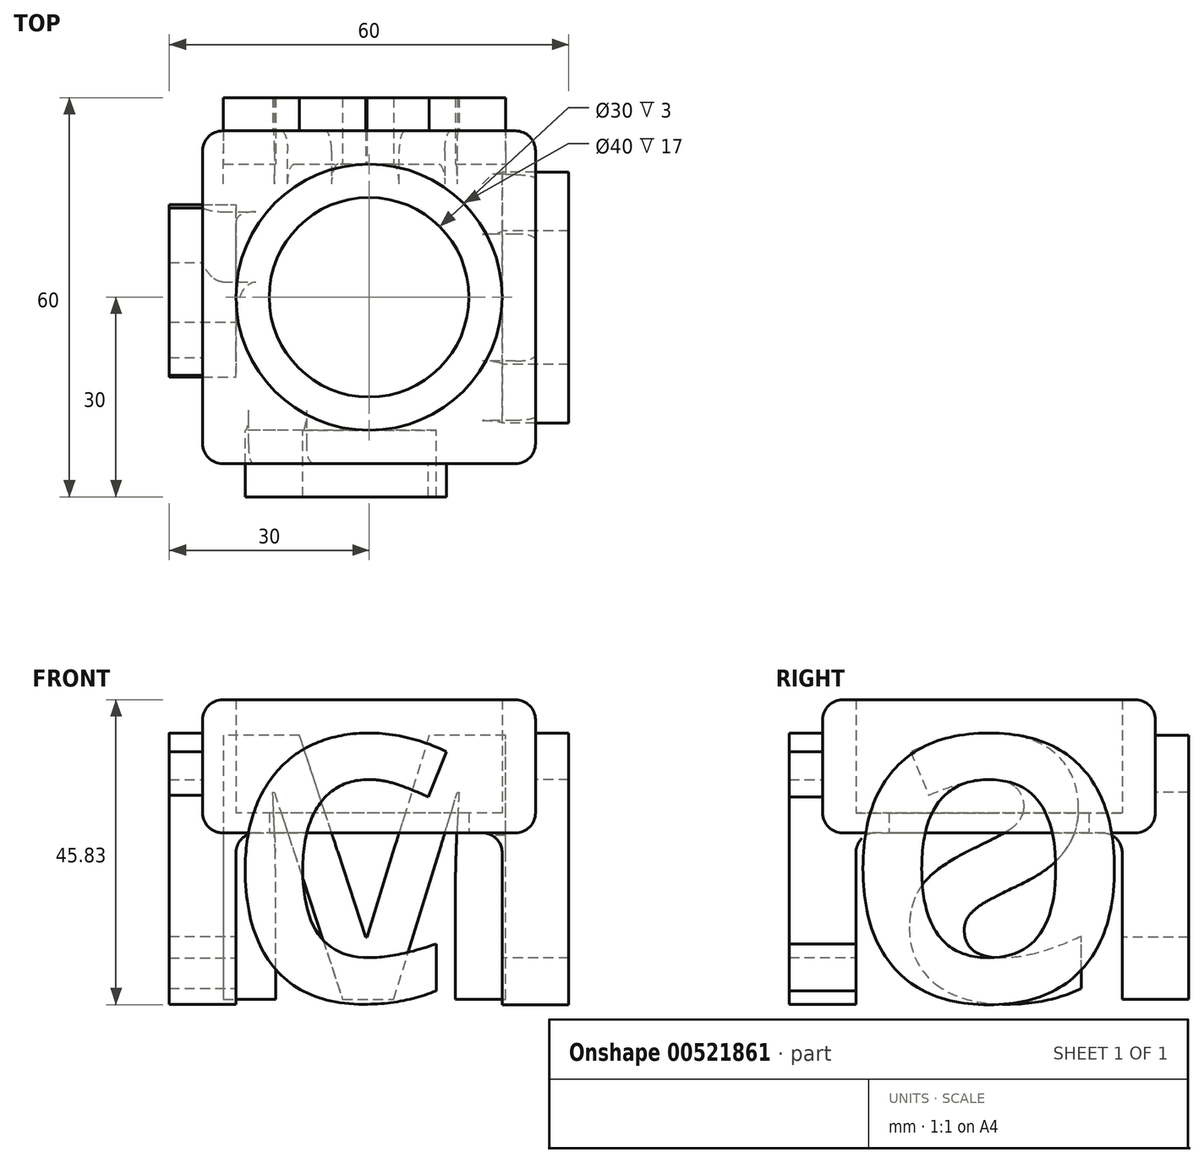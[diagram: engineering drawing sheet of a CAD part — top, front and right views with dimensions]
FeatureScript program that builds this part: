
annotation { "Feature Type Name" : "Feature", "Feature Type Description" : "" }
export const myFeature = defineFeature(function(context is Context, id is Id, definition is map)
    precondition{}
    {
        {
            var Q0;
            Q0=qCreatedBy(makeId("Top.planeOp"),FACE);
            var sketch = newSketch(context, id + "F0", { "sketchPlane" : qUnion([Q0])});
            skLineSegment(sketch, "E0.bottom", {"start": v(-25, 25) * mm, "end": v(25, 25) * mm});
            skLineSegment(sketch, "E0.top", {"start": v(-25, -25) * mm, "end": v(25, -25) * mm});
            skLineSegment(sketch, "E0.left", {"start": v(-25, 25) * mm, "end": v(-25, -25) * mm});
            skLineSegment(sketch, "E0.right", {"start": v(25, 25) * mm, "end": v(25, -25) * mm});
            skLineSegment(sketch, "E1", {"start": v(0, 25) * mm, "end": v(0, -25) * mm, "construction": true});
            skLineSegment(sketch, "E2", {"start": v(-25, 0) * mm, "end": v(25, 0) * mm, "construction": true});
            skCircle(sketch, "E3", {"center": v(0, 0) * mm, "radius": 15 * mm});
            skSolve(sketch);
        }
        {
            var Q0;
            Q0=makeQuery(id+"F0.imprint","IMPRINT",FACE,{"disambiguationData":[TD([[makeQuery(id+"F0.imprint","IMPRINT",EDGE,{"derivedFrom":sQuery(id+"F0.wireOp",EDGE,"E0.bottom")}),-1.0]])]});
            extrude(context, id + "F1", {"entities" : qUnion([Q0]), "depth" : 20 * mm, "offsetDistance" : 25 * mm});
        }
        {
            var Q0;
            Q0=qCreatedBy(makeId("Top.planeOp"),FACE);
            var sketch = newSketch(context, id + "F2", { "sketchPlane" : qUnion([Q0])});
            skCircle(sketch, "E4", {"center": v(0, 0) * mm, "radius": 20 * mm});
            skSolve(sketch);
        }
        {
            var Q0;
            Q0=qSketchRegion(id+"F2",true);
            extrude(context, id + "F3", {"entities" : qUnion([Q0]), "depth" : 20 * mm, "offsetDistance" : 25 * mm});
        }
        {
            var Q0;
            Q0=makeQuery(id+"F3.opExtrude","SWEPT_BODY",BODY,{"disambiguationData":[OSD([sQuery(id+"F2.wireOp",EDGE,"E4")])]});
            transform(context, id + "F4", {"entities" : qUnion([Q0]), "transformType" : TransformType.TRANSLATION_3D, "dx" : 0 * mm, "dy" : 0 * mm, "dz" : 3 * mm, "makeCopy" : false});
        }
        {
            var Q0;
            Q0=makeQuery(id+"F3.opExtrude","SWEPT_BODY",BODY,{"disambiguationData":[OSD([sQuery(id+"F2.wireOp",EDGE,"E4")])]});
            var Q1;
            Q1=makeQuery(id+"F1.opExtrude","SWEPT_BODY",BODY,{"disambiguationData":[OSD([sQuery(id+"F0.wireOp",EDGE,"E0.bottom"),sQuery(id+"F0.wireOp",EDGE,"E0.top"),sQuery(id+"F0.wireOp",EDGE,"E0.left"),sQuery(id+"F0.wireOp",EDGE,"E0.right"),sQuery(id+"F0.wireOp",EDGE,"E3")])]});
            booleanBodies(context, id + "F5", {"operationType" : BooleanOperationType.SUBTRACTION, "tools" : qUnion([Q0]), "targets" : qUnion([Q1])});
        }
        {
            var Q0;
            Q0=makeQuery(id+"F1.opExtrude","CAP_EDGE",EDGE,{"disambiguationData":[OSD([sQuery(id+"F0.wireOp",EDGE,"E0.bottom")])],"isStart":true});
            var Q1;
            Q1=makeQuery(id+"F1.opExtrude","SWEPT_EDGE",EDGE,{"disambiguationData":[OSD([sQuery(id+"F0.wireOp",EDGE,"E0.top"),sQuery(id+"F0.wireOp",EDGE,"E0.left")])]});
            var Q2;
            Q2=makeQuery(id+"F1.opExtrude","CAP_EDGE",EDGE,{"disambiguationData":[OSD([sQuery(id+"F0.wireOp",EDGE,"E0.top")])],"isStart":false});
            var Q3;
            Q3=makeQuery(id+"F1.opExtrude","CAP_EDGE",EDGE,{"disambiguationData":[OSD([sQuery(id+"F0.wireOp",EDGE,"E0.left")])],"isStart":false});
            var Q4;
            Q4=makeQuery(id+"F1.opExtrude","SWEPT_EDGE",EDGE,{"disambiguationData":[OSD([sQuery(id+"F0.wireOp",EDGE,"E0.bottom"),sQuery(id+"F0.wireOp",EDGE,"E0.right")])]});
            var Q5;
            Q5=makeQuery(id+"F1.opExtrude","SWEPT_EDGE",EDGE,{"disambiguationData":[OSD([sQuery(id+"F0.wireOp",EDGE,"E0.top"),sQuery(id+"F0.wireOp",EDGE,"E0.right")])]});
            var Q6;
            Q6=makeQuery(id+"F1.opExtrude","CAP_EDGE",EDGE,{"disambiguationData":[OSD([sQuery(id+"F0.wireOp",EDGE,"E0.right")])],"isStart":true});
            var Q7;
            Q7=makeQuery(id+"F1.opExtrude","CAP_EDGE",EDGE,{"disambiguationData":[OSD([sQuery(id+"F0.wireOp",EDGE,"E0.top")])],"isStart":true});
            var Q8;
            Q8=makeQuery(id+"F1.opExtrude","SWEPT_EDGE",EDGE,{"disambiguationData":[OSD([sQuery(id+"F0.wireOp",EDGE,"E0.bottom"),sQuery(id+"F0.wireOp",EDGE,"E0.left")])]});
            var Q9;
            Q9=makeQuery(id+"F1.opExtrude","CAP_EDGE",EDGE,{"disambiguationData":[OSD([sQuery(id+"F0.wireOp",EDGE,"E0.left")])],"isStart":true});
            var Q10;
            Q10=makeQuery(id+"F1.opExtrude","CAP_EDGE",EDGE,{"disambiguationData":[OSD([sQuery(id+"F0.wireOp",EDGE,"E0.bottom")])],"isStart":false});
            var Q11;
            Q11=makeQuery(id+"F1.opExtrude","CAP_EDGE",EDGE,{"disambiguationData":[OSD([sQuery(id+"F0.wireOp",EDGE,"E0.right")])],"isStart":false});
            fillet(context, id + "F6", {"entities" : qUnion([Q0, Q1, Q2, Q3, Q4, Q5, Q6, Q7, Q8, Q9, Q10, Q11]), "radius" : 3 * mm, "tangentPropagation" : true, "allowEdgeOverflow" : false});
        }
        {
            var Q0;
            Q0=makeQuery(id+"F1.opExtrude","SWEPT_FACE",FACE,{"disambiguationData":[OSD([sQuery(id+"F0.wireOp",EDGE,"E0.right")])]});
            var sketch = newSketch(context, id + "F7", { "sketchPlane" : qUnion([Q0])});
            skText(sketch, "E5", { "text": "O", "fontName": "OpenSans-Bold.ttf"});
            const initialGuessF7  = {"E5": [-0.02023, -0.07618, 1, 0, 0.04]};
            skSetInitialGuess(sketch, initialGuessF7);
            skSolve(sketch);
        }
        {
            var Q0;
            Q0=makeQuery(id+"F1.opExtrude","SWEPT_FACE",FACE,{"disambiguationData":[OSD([sQuery(id+"F0.wireOp",EDGE,"E0.top")])]});
            var sketch = newSketch(context, id + "F8", { "sketchPlane" : qUnion([Q0])});
            skText(sketch, "E6", { "text": "C", "fontName": "OpenSans-Bold.ttf"});
            const initialGuessF8  = {"E6": [-0.0744, -0.02372, 1, 0, 0.04]};
            skSetInitialGuess(sketch, initialGuessF8);
            skSolve(sketch);
        }
        {
            var Q0;
            Q0=makeQuery(id+"F1.opExtrude","SWEPT_FACE",FACE,{"disambiguationData":[OSD([sQuery(id+"F0.wireOp",EDGE,"E0.bottom")])]});
            var sketch = newSketch(context, id + "F9", { "sketchPlane" : qUnion([Q0])});
            skText(sketch, "E7", { "text": "M", "fontName": "OpenSans-Bold.ttf"});
            const initialGuessF9  = {"E7": [-0.02416, -0.08253, 1, 0, 0.04]};
            skSetInitialGuess(sketch, initialGuessF9);
            skSolve(sketch);
        }
        {
            var Q0;
            Q0=makeQuery(id+"F1.opExtrude","SWEPT_FACE",FACE,{"disambiguationData":[OSD([sQuery(id+"F0.wireOp",EDGE,"E0.left")])]});
            var sketch = newSketch(context, id + "F10", { "sketchPlane" : qUnion([Q0])});
            skText(sketch, "E8", { "text": "S", "fontName": "OpenSans-Bold.ttf"});
            const initialGuessF10  = {"E8": [-0.01252, -0.0554, 1, 0, 0.04]};
            skSetInitialGuess(sketch, initialGuessF10);
            skSolve(sketch);
        }
        {
            var Q0;
            Q0 = qSketchRegion(id + "F8", true);
            extrude(context, id + "F11", {"entities" : qUnion([Q0]), "depth" : 10 * mm, "offsetDistance" : 25 * mm});
        }
        {
            var Q0;
            Q0=makeQuery(id+"F7.imprint","IMPRINT",FACE,{"disambiguationData":[TD([[makeQuery(id+"F7.imprint","IMPRINT",EDGE,{"derivedFrom":sQuery(id+"F7.wireOp",EDGE,"E5.sketch_text.stroke-0")}),-1.0]])]});
            extrude(context, id + "F12", {"entities" : qUnion([Q0]), "depth" : 10 * mm, "offsetDistance" : 25 * mm});
        }
        {
            var Q0;
            Q0 = qSketchRegion(id + "F9", true);
            extrude(context, id + "F13", {"entities" : qUnion([Q0]), "depth" : 10 * mm, "offsetDistance" : 25 * mm});
        }
        {
            var Q0;
            Q0 = qSketchRegion(id + "F10", true);
            extrude(context, id + "F14", {"entities" : qUnion([Q0]), "depth" : 10 * mm, "offsetDistance" : 25 * mm});
        }
        {
            var Q0;
            Q0=makeQuery(id+"F11.opExtrude","SWEPT_BODY",BODY,{"disambiguationData":[OSD([sQuery(id+"F8.wireOp",EDGE,"E6.sketch_text.stroke-0"),sQuery(id+"F8.wireOp",EDGE,"E6.sketch_text.stroke-1"),sQuery(id+"F8.wireOp",EDGE,"E6.sketch_text.stroke-2"),sQuery(id+"F8.wireOp",EDGE,"E6.sketch_text.stroke-3"),sQuery(id+"F8.wireOp",EDGE,"E6.sketch_text.stroke-4"),sQuery(id+"F8.wireOp",EDGE,"E6.sketch_text.stroke-5"),sQuery(id+"F8.wireOp",EDGE,"E6.sketch_text.stroke-6"),sQuery(id+"F8.wireOp",EDGE,"E6.sketch_text.stroke-7"),sQuery(id+"F8.wireOp",EDGE,"E6.sketch_text.stroke-8"),sQuery(id+"F8.wireOp",EDGE,"E6.sketch_text.stroke-9"),sQuery(id+"F8.wireOp",EDGE,"E6.sketch_text.stroke-10"),sQuery(id+"F8.wireOp",EDGE,"E6.sketch_text.stroke-11"),sQuery(id+"F8.wireOp",EDGE,"E6.sketch_text.stroke-12"),sQuery(id+"F8.wireOp",EDGE,"E6.sketch_text.stroke-13"),sQuery(id+"F8.wireOp",EDGE,"E6.sketch_text.stroke-14")])]});
            var Q1;
            Q1=makeQuery(id+"F11.opExtrude","CAP_VERTEX",VERTEX,{"disambiguationData":[OSD([sQuery(id+"F8.wireOp",EDGE,"E6.sketch_text.stroke-10"),sQuery(id+"F8.wireOp",EDGE,"E6.sketch_text.stroke-11")])],"isStart":true});
            var Q2;
            Q2=sQuery(id+"F0.wireOp",VERTEX,"E1.end");
            transform(context, id + "F15", {"entities" : qUnion([Q0]), "transformType" : TransformType.TRANSLATION_ENTITY, "oppositeDirectionEntity" : false, "transformLine" : qUnion([Q1, Q2]), "makeCopy" : false});
        }
        {
            var Q0;
            Q0=makeQuery(id+"F12.opExtrude","SWEPT_BODY",BODY,{"disambiguationData":[OSD([sQuery(id+"F7.wireOp",EDGE,"E5.sketch_text.stroke-0"),sQuery(id+"F7.wireOp",EDGE,"E5.sketch_text.stroke-1"),sQuery(id+"F7.wireOp",EDGE,"E5.sketch_text.stroke-2"),sQuery(id+"F7.wireOp",EDGE,"E5.sketch_text.stroke-3"),sQuery(id+"F7.wireOp",EDGE,"E5.sketch_text.stroke-4"),sQuery(id+"F7.wireOp",EDGE,"E5.sketch_text.stroke-5"),sQuery(id+"F7.wireOp",EDGE,"E5.sketch_text.stroke-6"),sQuery(id+"F7.wireOp",EDGE,"E5.sketch_text.stroke-7"),sQuery(id+"F7.wireOp",EDGE,"E5.sketch_text.stroke-8"),sQuery(id+"F7.wireOp",EDGE,"E5.sketch_text.stroke-9"),sQuery(id+"F7.wireOp",EDGE,"E5.sketch_text.stroke-10"),sQuery(id+"F7.wireOp",EDGE,"E5.sketch_text.stroke-11"),sQuery(id+"F7.wireOp",EDGE,"E5.sketch_text.stroke-12"),sQuery(id+"F7.wireOp",EDGE,"E5.sketch_text.stroke-13")])]});
            var Q1;
            Q1=makeQuery(id+"F12.opExtrude","CAP_VERTEX",VERTEX,{"disambiguationData":[OSD([sQuery(id+"F7.wireOp",EDGE,"E5.sketch_text.stroke-5"),sQuery(id+"F7.wireOp",EDGE,"E5.sketch_text.stroke-6")])],"isStart":true});
            var Q2;
            Q2=sQuery(id+"F0.wireOp",VERTEX,"E2.end");
            transform(context, id + "F16", {"entities" : qUnion([Q0]), "transformType" : TransformType.TRANSLATION_ENTITY, "oppositeDirectionEntity" : false, "transformLine" : qUnion([Q1, Q2]), "makeCopy" : false});
        }
        {
            var Q0;
            Q0=makeQuery(id+"F13.opExtrude","SWEPT_BODY",BODY,{"disambiguationData":[OSD([sQuery(id+"F9.wireOp",EDGE,"E7.sketch_text.stroke-0"),sQuery(id+"F9.wireOp",EDGE,"E7.sketch_text.stroke-1"),sQuery(id+"F9.wireOp",EDGE,"E7.sketch_text.stroke-2"),sQuery(id+"F9.wireOp",EDGE,"E7.sketch_text.stroke-3"),sQuery(id+"F9.wireOp",EDGE,"E7.sketch_text.stroke-4"),sQuery(id+"F9.wireOp",EDGE,"E7.sketch_text.stroke-5"),sQuery(id+"F9.wireOp",EDGE,"E7.sketch_text.stroke-6"),sQuery(id+"F9.wireOp",EDGE,"E7.sketch_text.stroke-7"),sQuery(id+"F9.wireOp",EDGE,"E7.sketch_text.stroke-8"),sQuery(id+"F9.wireOp",EDGE,"E7.sketch_text.stroke-9"),sQuery(id+"F9.wireOp",EDGE,"E7.sketch_text.stroke-10"),sQuery(id+"F9.wireOp",EDGE,"E7.sketch_text.stroke-11"),sQuery(id+"F9.wireOp",EDGE,"E7.sketch_text.stroke-12"),sQuery(id+"F9.wireOp",EDGE,"E7.sketch_text.stroke-13"),sQuery(id+"F9.wireOp",EDGE,"E7.sketch_text.stroke-14"),sQuery(id+"F9.wireOp",EDGE,"E7.sketch_text.stroke-15"),sQuery(id+"F9.wireOp",EDGE,"E7.sketch_text.stroke-16"),sQuery(id+"F9.wireOp",EDGE,"E7.sketch_text.stroke-17"),sQuery(id+"F9.wireOp",EDGE,"E7.sketch_text.stroke-18")])]});
            var Q1;
            Q1=sQuery(id+"F9.wireOp",VERTEX,"E7.sketch_text.center.end");
            var Q2;
            Q2=sQuery(id+"F0.wireOp",VERTEX,"E1.start");
            transform(context, id + "F17", {"entities" : qUnion([Q0]), "transformType" : TransformType.TRANSLATION_ENTITY, "oppositeDirectionEntity" : false, "transformLine" : qUnion([Q1, Q2]), "makeCopy" : false});
        }
        {
            var Q0;
            Q0=makeQuery(id+"F14.opExtrude","SWEPT_BODY",BODY,{"disambiguationData":[OSD([sQuery(id+"F10.wireOp",EDGE,"E8.sketch_text.stroke-0"),sQuery(id+"F10.wireOp",EDGE,"E8.sketch_text.stroke-1"),sQuery(id+"F10.wireOp",EDGE,"E8.sketch_text.stroke-2"),sQuery(id+"F10.wireOp",EDGE,"E8.sketch_text.stroke-3"),sQuery(id+"F10.wireOp",EDGE,"E8.sketch_text.stroke-4"),sQuery(id+"F10.wireOp",EDGE,"E8.sketch_text.stroke-5"),sQuery(id+"F10.wireOp",EDGE,"E8.sketch_text.stroke-6"),sQuery(id+"F10.wireOp",EDGE,"E8.sketch_text.stroke-7"),sQuery(id+"F10.wireOp",EDGE,"E8.sketch_text.stroke-8"),sQuery(id+"F10.wireOp",EDGE,"E8.sketch_text.stroke-9"),sQuery(id+"F10.wireOp",EDGE,"E8.sketch_text.stroke-10"),sQuery(id+"F10.wireOp",EDGE,"E8.sketch_text.stroke-11"),sQuery(id+"F10.wireOp",EDGE,"E8.sketch_text.stroke-12"),sQuery(id+"F10.wireOp",EDGE,"E8.sketch_text.stroke-13"),sQuery(id+"F10.wireOp",EDGE,"E8.sketch_text.stroke-14"),sQuery(id+"F10.wireOp",EDGE,"E8.sketch_text.stroke-15"),sQuery(id+"F10.wireOp",EDGE,"E8.sketch_text.stroke-16"),sQuery(id+"F10.wireOp",EDGE,"E8.sketch_text.stroke-17"),sQuery(id+"F10.wireOp",EDGE,"E8.sketch_text.stroke-18"),sQuery(id+"F10.wireOp",EDGE,"E8.sketch_text.stroke-19"),sQuery(id+"F10.wireOp",EDGE,"E8.sketch_text.stroke-20"),sQuery(id+"F10.wireOp",EDGE,"E8.sketch_text.stroke-21"),sQuery(id+"F10.wireOp",EDGE,"E8.sketch_text.stroke-22"),sQuery(id+"F10.wireOp",EDGE,"E8.sketch_text.stroke-23"),sQuery(id+"F10.wireOp",EDGE,"E8.sketch_text.stroke-24"),sQuery(id+"F10.wireOp",EDGE,"E8.sketch_text.stroke-25"),sQuery(id+"F10.wireOp",EDGE,"E8.sketch_text.stroke-26"),sQuery(id+"F10.wireOp",EDGE,"E8.sketch_text.stroke-27")])]});
            var Q1;
            Q1=makeQuery(id+"F14.opExtrude","CAP_VERTEX",VERTEX,{"disambiguationData":[OSD([sQuery(id+"F10.wireOp",EDGE,"E8.sketch_text.stroke-15"),sQuery(id+"F10.wireOp",EDGE,"E8.sketch_text.stroke-16")])],"isStart":true});
            var Q2;
            Q2=sQuery(id+"F0.wireOp",VERTEX,"E2.start");
            transform(context, id + "F18", {"entities" : qUnion([Q0]), "transformType" : TransformType.TRANSLATION_ENTITY, "oppositeDirectionEntity" : false, "transformLine" : qUnion([Q1, Q2]), "makeCopy" : false});
        }
        {
            var Q0;
            Q0=makeQuery(id+"F11.opExtrude","SWEPT_BODY",BODY,{"disambiguationData":[OSD([sQuery(id+"F8.wireOp",EDGE,"E6.sketch_text.stroke-0"),sQuery(id+"F8.wireOp",EDGE,"E6.sketch_text.stroke-1"),sQuery(id+"F8.wireOp",EDGE,"E6.sketch_text.stroke-2"),sQuery(id+"F8.wireOp",EDGE,"E6.sketch_text.stroke-3"),sQuery(id+"F8.wireOp",EDGE,"E6.sketch_text.stroke-4"),sQuery(id+"F8.wireOp",EDGE,"E6.sketch_text.stroke-5"),sQuery(id+"F8.wireOp",EDGE,"E6.sketch_text.stroke-6"),sQuery(id+"F8.wireOp",EDGE,"E6.sketch_text.stroke-7"),sQuery(id+"F8.wireOp",EDGE,"E6.sketch_text.stroke-8"),sQuery(id+"F8.wireOp",EDGE,"E6.sketch_text.stroke-9"),sQuery(id+"F8.wireOp",EDGE,"E6.sketch_text.stroke-10"),sQuery(id+"F8.wireOp",EDGE,"E6.sketch_text.stroke-11"),sQuery(id+"F8.wireOp",EDGE,"E6.sketch_text.stroke-12"),sQuery(id+"F8.wireOp",EDGE,"E6.sketch_text.stroke-13"),sQuery(id+"F8.wireOp",EDGE,"E6.sketch_text.stroke-14")])]});
            transform(context, id + "F19", {"entities" : qUnion([Q0]), "transformType" : TransformType.TRANSLATION_3D, "dx" : 0 * mm, "dy" : 5 * mm, "dz" : 15 * mm, "makeCopy" : false});
        }
        {
            var Q0;
            Q0=makeQuery(id+"F12.opExtrude","SWEPT_BODY",BODY,{"disambiguationData":[OSD([sQuery(id+"F7.wireOp",EDGE,"E5.sketch_text.stroke-0"),sQuery(id+"F7.wireOp",EDGE,"E5.sketch_text.stroke-1"),sQuery(id+"F7.wireOp",EDGE,"E5.sketch_text.stroke-2"),sQuery(id+"F7.wireOp",EDGE,"E5.sketch_text.stroke-3"),sQuery(id+"F7.wireOp",EDGE,"E5.sketch_text.stroke-4"),sQuery(id+"F7.wireOp",EDGE,"E5.sketch_text.stroke-5"),sQuery(id+"F7.wireOp",EDGE,"E5.sketch_text.stroke-6"),sQuery(id+"F7.wireOp",EDGE,"E5.sketch_text.stroke-7"),sQuery(id+"F7.wireOp",EDGE,"E5.sketch_text.stroke-8"),sQuery(id+"F7.wireOp",EDGE,"E5.sketch_text.stroke-9"),sQuery(id+"F7.wireOp",EDGE,"E5.sketch_text.stroke-10"),sQuery(id+"F7.wireOp",EDGE,"E5.sketch_text.stroke-11"),sQuery(id+"F7.wireOp",EDGE,"E5.sketch_text.stroke-12"),sQuery(id+"F7.wireOp",EDGE,"E5.sketch_text.stroke-13")])]});
            transform(context, id + "F20", {"entities" : qUnion([Q0]), "transformType" : TransformType.TRANSLATION_3D, "dx" : -5 * mm, "dy" : 0 * mm, "dz" : 15 * mm, "makeCopy" : false});
        }
        {
            var Q0;
            Q0=makeQuery(id+"F13.opExtrude","SWEPT_BODY",BODY,{"disambiguationData":[OSD([sQuery(id+"F9.wireOp",EDGE,"E7.sketch_text.stroke-0"),sQuery(id+"F9.wireOp",EDGE,"E7.sketch_text.stroke-1"),sQuery(id+"F9.wireOp",EDGE,"E7.sketch_text.stroke-2"),sQuery(id+"F9.wireOp",EDGE,"E7.sketch_text.stroke-3"),sQuery(id+"F9.wireOp",EDGE,"E7.sketch_text.stroke-4"),sQuery(id+"F9.wireOp",EDGE,"E7.sketch_text.stroke-5"),sQuery(id+"F9.wireOp",EDGE,"E7.sketch_text.stroke-6"),sQuery(id+"F9.wireOp",EDGE,"E7.sketch_text.stroke-7"),sQuery(id+"F9.wireOp",EDGE,"E7.sketch_text.stroke-8"),sQuery(id+"F9.wireOp",EDGE,"E7.sketch_text.stroke-9"),sQuery(id+"F9.wireOp",EDGE,"E7.sketch_text.stroke-10"),sQuery(id+"F9.wireOp",EDGE,"E7.sketch_text.stroke-11"),sQuery(id+"F9.wireOp",EDGE,"E7.sketch_text.stroke-12"),sQuery(id+"F9.wireOp",EDGE,"E7.sketch_text.stroke-13"),sQuery(id+"F9.wireOp",EDGE,"E7.sketch_text.stroke-14"),sQuery(id+"F9.wireOp",EDGE,"E7.sketch_text.stroke-15"),sQuery(id+"F9.wireOp",EDGE,"E7.sketch_text.stroke-16"),sQuery(id+"F9.wireOp",EDGE,"E7.sketch_text.stroke-17"),sQuery(id+"F9.wireOp",EDGE,"E7.sketch_text.stroke-18")])]});
            transform(context, id + "F21", {"entities" : qUnion([Q0]), "transformType" : TransformType.TRANSLATION_3D, "dx" : 0 * mm, "dy" : -5 * mm, "dz" : 15 * mm, "makeCopy" : false});
        }
        {
            var Q0;
            Q0=makeQuery(id+"F14.opExtrude","SWEPT_BODY",BODY,{"disambiguationData":[OSD([sQuery(id+"F10.wireOp",EDGE,"E8.sketch_text.stroke-0"),sQuery(id+"F10.wireOp",EDGE,"E8.sketch_text.stroke-1"),sQuery(id+"F10.wireOp",EDGE,"E8.sketch_text.stroke-2"),sQuery(id+"F10.wireOp",EDGE,"E8.sketch_text.stroke-3"),sQuery(id+"F10.wireOp",EDGE,"E8.sketch_text.stroke-4"),sQuery(id+"F10.wireOp",EDGE,"E8.sketch_text.stroke-5"),sQuery(id+"F10.wireOp",EDGE,"E8.sketch_text.stroke-6"),sQuery(id+"F10.wireOp",EDGE,"E8.sketch_text.stroke-7"),sQuery(id+"F10.wireOp",EDGE,"E8.sketch_text.stroke-8"),sQuery(id+"F10.wireOp",EDGE,"E8.sketch_text.stroke-9"),sQuery(id+"F10.wireOp",EDGE,"E8.sketch_text.stroke-10"),sQuery(id+"F10.wireOp",EDGE,"E8.sketch_text.stroke-11"),sQuery(id+"F10.wireOp",EDGE,"E8.sketch_text.stroke-12"),sQuery(id+"F10.wireOp",EDGE,"E8.sketch_text.stroke-13"),sQuery(id+"F10.wireOp",EDGE,"E8.sketch_text.stroke-14"),sQuery(id+"F10.wireOp",EDGE,"E8.sketch_text.stroke-15"),sQuery(id+"F10.wireOp",EDGE,"E8.sketch_text.stroke-16"),sQuery(id+"F10.wireOp",EDGE,"E8.sketch_text.stroke-17"),sQuery(id+"F10.wireOp",EDGE,"E8.sketch_text.stroke-18"),sQuery(id+"F10.wireOp",EDGE,"E8.sketch_text.stroke-19"),sQuery(id+"F10.wireOp",EDGE,"E8.sketch_text.stroke-20"),sQuery(id+"F10.wireOp",EDGE,"E8.sketch_text.stroke-21"),sQuery(id+"F10.wireOp",EDGE,"E8.sketch_text.stroke-22"),sQuery(id+"F10.wireOp",EDGE,"E8.sketch_text.stroke-23"),sQuery(id+"F10.wireOp",EDGE,"E8.sketch_text.stroke-24"),sQuery(id+"F10.wireOp",EDGE,"E8.sketch_text.stroke-25"),sQuery(id+"F10.wireOp",EDGE,"E8.sketch_text.stroke-26"),sQuery(id+"F10.wireOp",EDGE,"E8.sketch_text.stroke-27")])]});
            transform(context, id + "F22", {"entities" : qUnion([Q0]), "transformType" : TransformType.TRANSLATION_3D, "dx" : 5 * mm, "dy" : 0 * mm, "dz" : 15 * mm, "makeCopy" : false});
        }
        {
            var Q0;
            Q0=makeQuery(id+"F13.opExtrude","SWEPT_BODY",BODY,{"disambiguationData":[OSD([sQuery(id+"F9.wireOp",EDGE,"E7.sketch_text.stroke-0"),sQuery(id+"F9.wireOp",EDGE,"E7.sketch_text.stroke-1"),sQuery(id+"F9.wireOp",EDGE,"E7.sketch_text.stroke-2"),sQuery(id+"F9.wireOp",EDGE,"E7.sketch_text.stroke-3"),sQuery(id+"F9.wireOp",EDGE,"E7.sketch_text.stroke-4"),sQuery(id+"F9.wireOp",EDGE,"E7.sketch_text.stroke-5"),sQuery(id+"F9.wireOp",EDGE,"E7.sketch_text.stroke-6"),sQuery(id+"F9.wireOp",EDGE,"E7.sketch_text.stroke-7"),sQuery(id+"F9.wireOp",EDGE,"E7.sketch_text.stroke-8"),sQuery(id+"F9.wireOp",EDGE,"E7.sketch_text.stroke-9"),sQuery(id+"F9.wireOp",EDGE,"E7.sketch_text.stroke-10"),sQuery(id+"F9.wireOp",EDGE,"E7.sketch_text.stroke-11"),sQuery(id+"F9.wireOp",EDGE,"E7.sketch_text.stroke-12"),sQuery(id+"F9.wireOp",EDGE,"E7.sketch_text.stroke-13"),sQuery(id+"F9.wireOp",EDGE,"E7.sketch_text.stroke-14"),sQuery(id+"F9.wireOp",EDGE,"E7.sketch_text.stroke-15"),sQuery(id+"F9.wireOp",EDGE,"E7.sketch_text.stroke-16"),sQuery(id+"F9.wireOp",EDGE,"E7.sketch_text.stroke-17"),sQuery(id+"F9.wireOp",EDGE,"E7.sketch_text.stroke-18")])]});
            var Q1;
            Q1=makeQuery(id+"F11.opExtrude","SWEPT_BODY",BODY,{"disambiguationData":[OSD([sQuery(id+"F8.wireOp",EDGE,"E6.sketch_text.stroke-0"),sQuery(id+"F8.wireOp",EDGE,"E6.sketch_text.stroke-1"),sQuery(id+"F8.wireOp",EDGE,"E6.sketch_text.stroke-2"),sQuery(id+"F8.wireOp",EDGE,"E6.sketch_text.stroke-3"),sQuery(id+"F8.wireOp",EDGE,"E6.sketch_text.stroke-4"),sQuery(id+"F8.wireOp",EDGE,"E6.sketch_text.stroke-5"),sQuery(id+"F8.wireOp",EDGE,"E6.sketch_text.stroke-6"),sQuery(id+"F8.wireOp",EDGE,"E6.sketch_text.stroke-7"),sQuery(id+"F8.wireOp",EDGE,"E6.sketch_text.stroke-8"),sQuery(id+"F8.wireOp",EDGE,"E6.sketch_text.stroke-9"),sQuery(id+"F8.wireOp",EDGE,"E6.sketch_text.stroke-10"),sQuery(id+"F8.wireOp",EDGE,"E6.sketch_text.stroke-11"),sQuery(id+"F8.wireOp",EDGE,"E6.sketch_text.stroke-12"),sQuery(id+"F8.wireOp",EDGE,"E6.sketch_text.stroke-13"),sQuery(id+"F8.wireOp",EDGE,"E6.sketch_text.stroke-14")])]});
            var Q2;
            Q2=makeQuery(id+"F1.opExtrude","SWEPT_BODY",BODY,{"disambiguationData":[OSD([sQuery(id+"F0.wireOp",EDGE,"E0.bottom"),sQuery(id+"F0.wireOp",EDGE,"E0.top"),sQuery(id+"F0.wireOp",EDGE,"E0.left"),sQuery(id+"F0.wireOp",EDGE,"E0.right"),sQuery(id+"F0.wireOp",EDGE,"E3")])]});
            var Q3;
            Q3=makeQuery(id+"F14.opExtrude","SWEPT_BODY",BODY,{"disambiguationData":[OSD([sQuery(id+"F10.wireOp",EDGE,"E8.sketch_text.stroke-0"),sQuery(id+"F10.wireOp",EDGE,"E8.sketch_text.stroke-1"),sQuery(id+"F10.wireOp",EDGE,"E8.sketch_text.stroke-2"),sQuery(id+"F10.wireOp",EDGE,"E8.sketch_text.stroke-3"),sQuery(id+"F10.wireOp",EDGE,"E8.sketch_text.stroke-4"),sQuery(id+"F10.wireOp",EDGE,"E8.sketch_text.stroke-5"),sQuery(id+"F10.wireOp",EDGE,"E8.sketch_text.stroke-6"),sQuery(id+"F10.wireOp",EDGE,"E8.sketch_text.stroke-7"),sQuery(id+"F10.wireOp",EDGE,"E8.sketch_text.stroke-8"),sQuery(id+"F10.wireOp",EDGE,"E8.sketch_text.stroke-9"),sQuery(id+"F10.wireOp",EDGE,"E8.sketch_text.stroke-10"),sQuery(id+"F10.wireOp",EDGE,"E8.sketch_text.stroke-11"),sQuery(id+"F10.wireOp",EDGE,"E8.sketch_text.stroke-12"),sQuery(id+"F10.wireOp",EDGE,"E8.sketch_text.stroke-13"),sQuery(id+"F10.wireOp",EDGE,"E8.sketch_text.stroke-14"),sQuery(id+"F10.wireOp",EDGE,"E8.sketch_text.stroke-15"),sQuery(id+"F10.wireOp",EDGE,"E8.sketch_text.stroke-16"),sQuery(id+"F10.wireOp",EDGE,"E8.sketch_text.stroke-17"),sQuery(id+"F10.wireOp",EDGE,"E8.sketch_text.stroke-18"),sQuery(id+"F10.wireOp",EDGE,"E8.sketch_text.stroke-19"),sQuery(id+"F10.wireOp",EDGE,"E8.sketch_text.stroke-20"),sQuery(id+"F10.wireOp",EDGE,"E8.sketch_text.stroke-21"),sQuery(id+"F10.wireOp",EDGE,"E8.sketch_text.stroke-22"),sQuery(id+"F10.wireOp",EDGE,"E8.sketch_text.stroke-23"),sQuery(id+"F10.wireOp",EDGE,"E8.sketch_text.stroke-24"),sQuery(id+"F10.wireOp",EDGE,"E8.sketch_text.stroke-25"),sQuery(id+"F10.wireOp",EDGE,"E8.sketch_text.stroke-26"),sQuery(id+"F10.wireOp",EDGE,"E8.sketch_text.stroke-27")])]});
            var Q4;
            Q4=makeQuery(id+"F12.opExtrude","SWEPT_BODY",BODY,{"disambiguationData":[OSD([sQuery(id+"F7.wireOp",EDGE,"E5.sketch_text.stroke-0"),sQuery(id+"F7.wireOp",EDGE,"E5.sketch_text.stroke-1"),sQuery(id+"F7.wireOp",EDGE,"E5.sketch_text.stroke-2"),sQuery(id+"F7.wireOp",EDGE,"E5.sketch_text.stroke-3"),sQuery(id+"F7.wireOp",EDGE,"E5.sketch_text.stroke-4"),sQuery(id+"F7.wireOp",EDGE,"E5.sketch_text.stroke-5"),sQuery(id+"F7.wireOp",EDGE,"E5.sketch_text.stroke-6"),sQuery(id+"F7.wireOp",EDGE,"E5.sketch_text.stroke-7"),sQuery(id+"F7.wireOp",EDGE,"E5.sketch_text.stroke-8"),sQuery(id+"F7.wireOp",EDGE,"E5.sketch_text.stroke-9"),sQuery(id+"F7.wireOp",EDGE,"E5.sketch_text.stroke-10"),sQuery(id+"F7.wireOp",EDGE,"E5.sketch_text.stroke-11"),sQuery(id+"F7.wireOp",EDGE,"E5.sketch_text.stroke-12"),sQuery(id+"F7.wireOp",EDGE,"E5.sketch_text.stroke-13")])]});
            booleanBodies(context, id + "F23", {"operationType" : BooleanOperationType.UNION, "tools" : qUnion([Q0, Q1, Q2, Q3, Q4])});
        }
        {
            var Q0;
            Q0=makeQuery(id+"F23.opBoolean","INTERSECT",EDGE,{"derivedFrom":[makeQuery(id+"F1.opExtrude","CAP_FACE",FACE,{"disambiguationData":[OSD([sQuery(id+"F0.wireOp",EDGE,"E0.bottom"),sQuery(id+"F0.wireOp",EDGE,"E0.top"),sQuery(id+"F0.wireOp",EDGE,"E0.left"),sQuery(id+"F0.wireOp",EDGE,"E0.right"),sQuery(id+"F0.wireOp",EDGE,"E3")])],"isStart":true}),makeQuery(id+"F11.opExtrude","CAP_FACE",FACE,{"disambiguationData":[OSD([sQuery(id+"F8.wireOp",EDGE,"E6.sketch_text.stroke-0"),sQuery(id+"F8.wireOp",EDGE,"E6.sketch_text.stroke-1"),sQuery(id+"F8.wireOp",EDGE,"E6.sketch_text.stroke-2"),sQuery(id+"F8.wireOp",EDGE,"E6.sketch_text.stroke-3"),sQuery(id+"F8.wireOp",EDGE,"E6.sketch_text.stroke-4"),sQuery(id+"F8.wireOp",EDGE,"E6.sketch_text.stroke-5"),sQuery(id+"F8.wireOp",EDGE,"E6.sketch_text.stroke-6"),sQuery(id+"F8.wireOp",EDGE,"E6.sketch_text.stroke-7"),sQuery(id+"F8.wireOp",EDGE,"E6.sketch_text.stroke-8"),sQuery(id+"F8.wireOp",EDGE,"E6.sketch_text.stroke-9"),sQuery(id+"F8.wireOp",EDGE,"E6.sketch_text.stroke-10"),sQuery(id+"F8.wireOp",EDGE,"E6.sketch_text.stroke-11"),sQuery(id+"F8.wireOp",EDGE,"E6.sketch_text.stroke-12"),sQuery(id+"F8.wireOp",EDGE,"E6.sketch_text.stroke-13"),sQuery(id+"F8.wireOp",EDGE,"E6.sketch_text.stroke-14")])],"isStart":true})]});
            fillet(context, id + "F24", {"entities" : qUnion([Q0]), "radius" : 3 * mm, "tangentPropagation" : true, "allowEdgeOverflow" : false});
        }
        {
            var Q0;
            Q0=makeQuery(id+"F23.opBoolean","INTERSECT",EDGE,{"disambiguationData":[OD(1.0)],"derivedFrom":[makeQuery(id+"F1.opExtrude","CAP_FACE",FACE,{"disambiguationData":[OSD([sQuery(id+"F0.wireOp",EDGE,"E0.bottom"),sQuery(id+"F0.wireOp",EDGE,"E0.top"),sQuery(id+"F0.wireOp",EDGE,"E0.left"),sQuery(id+"F0.wireOp",EDGE,"E0.right"),sQuery(id+"F0.wireOp",EDGE,"E3")])],"isStart":true}),makeQuery(id+"F12.opExtrude","CAP_FACE",FACE,{"disambiguationData":[OSD([sQuery(id+"F7.wireOp",EDGE,"E5.sketch_text.stroke-0"),sQuery(id+"F7.wireOp",EDGE,"E5.sketch_text.stroke-1"),sQuery(id+"F7.wireOp",EDGE,"E5.sketch_text.stroke-2"),sQuery(id+"F7.wireOp",EDGE,"E5.sketch_text.stroke-3"),sQuery(id+"F7.wireOp",EDGE,"E5.sketch_text.stroke-4"),sQuery(id+"F7.wireOp",EDGE,"E5.sketch_text.stroke-5"),sQuery(id+"F7.wireOp",EDGE,"E5.sketch_text.stroke-6"),sQuery(id+"F7.wireOp",EDGE,"E5.sketch_text.stroke-7"),sQuery(id+"F7.wireOp",EDGE,"E5.sketch_text.stroke-8"),sQuery(id+"F7.wireOp",EDGE,"E5.sketch_text.stroke-9"),sQuery(id+"F7.wireOp",EDGE,"E5.sketch_text.stroke-10"),sQuery(id+"F7.wireOp",EDGE,"E5.sketch_text.stroke-11"),sQuery(id+"F7.wireOp",EDGE,"E5.sketch_text.stroke-12"),sQuery(id+"F7.wireOp",EDGE,"E5.sketch_text.stroke-13")])],"isStart":true})]});
            var Q1;
            Q1=makeQuery(id+"F23.opBoolean","INTERSECT",EDGE,{"disambiguationData":[OD(0.0)],"derivedFrom":[makeQuery(id+"F1.opExtrude","CAP_FACE",FACE,{"disambiguationData":[OSD([sQuery(id+"F0.wireOp",EDGE,"E0.bottom"),sQuery(id+"F0.wireOp",EDGE,"E0.top"),sQuery(id+"F0.wireOp",EDGE,"E0.left"),sQuery(id+"F0.wireOp",EDGE,"E0.right"),sQuery(id+"F0.wireOp",EDGE,"E3")])],"isStart":true}),makeQuery(id+"F12.opExtrude","CAP_FACE",FACE,{"disambiguationData":[OSD([sQuery(id+"F7.wireOp",EDGE,"E5.sketch_text.stroke-0"),sQuery(id+"F7.wireOp",EDGE,"E5.sketch_text.stroke-1"),sQuery(id+"F7.wireOp",EDGE,"E5.sketch_text.stroke-2"),sQuery(id+"F7.wireOp",EDGE,"E5.sketch_text.stroke-3"),sQuery(id+"F7.wireOp",EDGE,"E5.sketch_text.stroke-4"),sQuery(id+"F7.wireOp",EDGE,"E5.sketch_text.stroke-5"),sQuery(id+"F7.wireOp",EDGE,"E5.sketch_text.stroke-6"),sQuery(id+"F7.wireOp",EDGE,"E5.sketch_text.stroke-7"),sQuery(id+"F7.wireOp",EDGE,"E5.sketch_text.stroke-8"),sQuery(id+"F7.wireOp",EDGE,"E5.sketch_text.stroke-9"),sQuery(id+"F7.wireOp",EDGE,"E5.sketch_text.stroke-10"),sQuery(id+"F7.wireOp",EDGE,"E5.sketch_text.stroke-11"),sQuery(id+"F7.wireOp",EDGE,"E5.sketch_text.stroke-12"),sQuery(id+"F7.wireOp",EDGE,"E5.sketch_text.stroke-13")])],"isStart":true})]});
            fillet(context, id + "F25", {"entities" : qUnion([Q0, Q1]), "radius" : 3 * mm, "tangentPropagation" : true, "allowEdgeOverflow" : false});
        }
        {
            var Q0;
            Q0=makeQuery(id+"F23.opBoolean","INTERSECT",EDGE,{"disambiguationData":[OD(1.0)],"derivedFrom":[makeQuery(id+"F1.opExtrude","CAP_FACE",FACE,{"disambiguationData":[OSD([sQuery(id+"F0.wireOp",EDGE,"E0.bottom"),sQuery(id+"F0.wireOp",EDGE,"E0.top"),sQuery(id+"F0.wireOp",EDGE,"E0.left"),sQuery(id+"F0.wireOp",EDGE,"E0.right"),sQuery(id+"F0.wireOp",EDGE,"E3")])],"isStart":true}),makeQuery(id+"F13.opExtrude","CAP_FACE",FACE,{"disambiguationData":[OSD([sQuery(id+"F9.wireOp",EDGE,"E7.sketch_text.stroke-0"),sQuery(id+"F9.wireOp",EDGE,"E7.sketch_text.stroke-1"),sQuery(id+"F9.wireOp",EDGE,"E7.sketch_text.stroke-2"),sQuery(id+"F9.wireOp",EDGE,"E7.sketch_text.stroke-3"),sQuery(id+"F9.wireOp",EDGE,"E7.sketch_text.stroke-4"),sQuery(id+"F9.wireOp",EDGE,"E7.sketch_text.stroke-5"),sQuery(id+"F9.wireOp",EDGE,"E7.sketch_text.stroke-6"),sQuery(id+"F9.wireOp",EDGE,"E7.sketch_text.stroke-7"),sQuery(id+"F9.wireOp",EDGE,"E7.sketch_text.stroke-8"),sQuery(id+"F9.wireOp",EDGE,"E7.sketch_text.stroke-9"),sQuery(id+"F9.wireOp",EDGE,"E7.sketch_text.stroke-10"),sQuery(id+"F9.wireOp",EDGE,"E7.sketch_text.stroke-11"),sQuery(id+"F9.wireOp",EDGE,"E7.sketch_text.stroke-12"),sQuery(id+"F9.wireOp",EDGE,"E7.sketch_text.stroke-13"),sQuery(id+"F9.wireOp",EDGE,"E7.sketch_text.stroke-14"),sQuery(id+"F9.wireOp",EDGE,"E7.sketch_text.stroke-15"),sQuery(id+"F9.wireOp",EDGE,"E7.sketch_text.stroke-16"),sQuery(id+"F9.wireOp",EDGE,"E7.sketch_text.stroke-17"),sQuery(id+"F9.wireOp",EDGE,"E7.sketch_text.stroke-18")])],"isStart":true})]});
            var Q1;
            Q1=makeQuery(id+"F23.opBoolean","INTERSECT",EDGE,{"disambiguationData":[OD(2.0)],"derivedFrom":[makeQuery(id+"F1.opExtrude","CAP_FACE",FACE,{"disambiguationData":[OSD([sQuery(id+"F0.wireOp",EDGE,"E0.bottom"),sQuery(id+"F0.wireOp",EDGE,"E0.top"),sQuery(id+"F0.wireOp",EDGE,"E0.left"),sQuery(id+"F0.wireOp",EDGE,"E0.right"),sQuery(id+"F0.wireOp",EDGE,"E3")])],"isStart":true}),makeQuery(id+"F13.opExtrude","CAP_FACE",FACE,{"disambiguationData":[OSD([sQuery(id+"F9.wireOp",EDGE,"E7.sketch_text.stroke-0"),sQuery(id+"F9.wireOp",EDGE,"E7.sketch_text.stroke-1"),sQuery(id+"F9.wireOp",EDGE,"E7.sketch_text.stroke-2"),sQuery(id+"F9.wireOp",EDGE,"E7.sketch_text.stroke-3"),sQuery(id+"F9.wireOp",EDGE,"E7.sketch_text.stroke-4"),sQuery(id+"F9.wireOp",EDGE,"E7.sketch_text.stroke-5"),sQuery(id+"F9.wireOp",EDGE,"E7.sketch_text.stroke-6"),sQuery(id+"F9.wireOp",EDGE,"E7.sketch_text.stroke-7"),sQuery(id+"F9.wireOp",EDGE,"E7.sketch_text.stroke-8"),sQuery(id+"F9.wireOp",EDGE,"E7.sketch_text.stroke-9"),sQuery(id+"F9.wireOp",EDGE,"E7.sketch_text.stroke-10"),sQuery(id+"F9.wireOp",EDGE,"E7.sketch_text.stroke-11"),sQuery(id+"F9.wireOp",EDGE,"E7.sketch_text.stroke-12"),sQuery(id+"F9.wireOp",EDGE,"E7.sketch_text.stroke-13"),sQuery(id+"F9.wireOp",EDGE,"E7.sketch_text.stroke-14"),sQuery(id+"F9.wireOp",EDGE,"E7.sketch_text.stroke-15"),sQuery(id+"F9.wireOp",EDGE,"E7.sketch_text.stroke-16"),sQuery(id+"F9.wireOp",EDGE,"E7.sketch_text.stroke-17"),sQuery(id+"F9.wireOp",EDGE,"E7.sketch_text.stroke-18")])],"isStart":true})]});
            var Q2;
            Q2=makeQuery(id+"F23.opBoolean","INTERSECT",EDGE,{"disambiguationData":[OD(0.0)],"derivedFrom":[makeQuery(id+"F1.opExtrude","CAP_FACE",FACE,{"disambiguationData":[OSD([sQuery(id+"F0.wireOp",EDGE,"E0.bottom"),sQuery(id+"F0.wireOp",EDGE,"E0.top"),sQuery(id+"F0.wireOp",EDGE,"E0.left"),sQuery(id+"F0.wireOp",EDGE,"E0.right"),sQuery(id+"F0.wireOp",EDGE,"E3")])],"isStart":true}),makeQuery(id+"F13.opExtrude","CAP_FACE",FACE,{"disambiguationData":[OSD([sQuery(id+"F9.wireOp",EDGE,"E7.sketch_text.stroke-0"),sQuery(id+"F9.wireOp",EDGE,"E7.sketch_text.stroke-1"),sQuery(id+"F9.wireOp",EDGE,"E7.sketch_text.stroke-2"),sQuery(id+"F9.wireOp",EDGE,"E7.sketch_text.stroke-3"),sQuery(id+"F9.wireOp",EDGE,"E7.sketch_text.stroke-4"),sQuery(id+"F9.wireOp",EDGE,"E7.sketch_text.stroke-5"),sQuery(id+"F9.wireOp",EDGE,"E7.sketch_text.stroke-6"),sQuery(id+"F9.wireOp",EDGE,"E7.sketch_text.stroke-7"),sQuery(id+"F9.wireOp",EDGE,"E7.sketch_text.stroke-8"),sQuery(id+"F9.wireOp",EDGE,"E7.sketch_text.stroke-9"),sQuery(id+"F9.wireOp",EDGE,"E7.sketch_text.stroke-10"),sQuery(id+"F9.wireOp",EDGE,"E7.sketch_text.stroke-11"),sQuery(id+"F9.wireOp",EDGE,"E7.sketch_text.stroke-12"),sQuery(id+"F9.wireOp",EDGE,"E7.sketch_text.stroke-13"),sQuery(id+"F9.wireOp",EDGE,"E7.sketch_text.stroke-14"),sQuery(id+"F9.wireOp",EDGE,"E7.sketch_text.stroke-15"),sQuery(id+"F9.wireOp",EDGE,"E7.sketch_text.stroke-16"),sQuery(id+"F9.wireOp",EDGE,"E7.sketch_text.stroke-17"),sQuery(id+"F9.wireOp",EDGE,"E7.sketch_text.stroke-18")])],"isStart":true})]});
            var Q3;
            Q3=makeQuery(id+"F23.opBoolean","INTERSECT",EDGE,{"disambiguationData":[OD(3.0)],"derivedFrom":[makeQuery(id+"F1.opExtrude","CAP_FACE",FACE,{"disambiguationData":[OSD([sQuery(id+"F0.wireOp",EDGE,"E0.bottom"),sQuery(id+"F0.wireOp",EDGE,"E0.top"),sQuery(id+"F0.wireOp",EDGE,"E0.left"),sQuery(id+"F0.wireOp",EDGE,"E0.right"),sQuery(id+"F0.wireOp",EDGE,"E3")])],"isStart":true}),makeQuery(id+"F13.opExtrude","CAP_FACE",FACE,{"disambiguationData":[OSD([sQuery(id+"F9.wireOp",EDGE,"E7.sketch_text.stroke-0"),sQuery(id+"F9.wireOp",EDGE,"E7.sketch_text.stroke-1"),sQuery(id+"F9.wireOp",EDGE,"E7.sketch_text.stroke-2"),sQuery(id+"F9.wireOp",EDGE,"E7.sketch_text.stroke-3"),sQuery(id+"F9.wireOp",EDGE,"E7.sketch_text.stroke-4"),sQuery(id+"F9.wireOp",EDGE,"E7.sketch_text.stroke-5"),sQuery(id+"F9.wireOp",EDGE,"E7.sketch_text.stroke-6"),sQuery(id+"F9.wireOp",EDGE,"E7.sketch_text.stroke-7"),sQuery(id+"F9.wireOp",EDGE,"E7.sketch_text.stroke-8"),sQuery(id+"F9.wireOp",EDGE,"E7.sketch_text.stroke-9"),sQuery(id+"F9.wireOp",EDGE,"E7.sketch_text.stroke-10"),sQuery(id+"F9.wireOp",EDGE,"E7.sketch_text.stroke-11"),sQuery(id+"F9.wireOp",EDGE,"E7.sketch_text.stroke-12"),sQuery(id+"F9.wireOp",EDGE,"E7.sketch_text.stroke-13"),sQuery(id+"F9.wireOp",EDGE,"E7.sketch_text.stroke-14"),sQuery(id+"F9.wireOp",EDGE,"E7.sketch_text.stroke-15"),sQuery(id+"F9.wireOp",EDGE,"E7.sketch_text.stroke-16"),sQuery(id+"F9.wireOp",EDGE,"E7.sketch_text.stroke-17"),sQuery(id+"F9.wireOp",EDGE,"E7.sketch_text.stroke-18")])],"isStart":true})]});
            fillet(context, id + "F26", {"entities" : qUnion([Q0, Q1, Q2, Q3]), "radius" : 3 * mm, "tangentPropagation" : true, "allowEdgeOverflow" : false});
        }
        {
            var Q0;
            Q0=makeQuery(id+"F23.opBoolean","INTERSECT",EDGE,{"derivedFrom":[makeQuery(id+"F1.opExtrude","CAP_FACE",FACE,{"disambiguationData":[OSD([sQuery(id+"F0.wireOp",EDGE,"E0.bottom"),sQuery(id+"F0.wireOp",EDGE,"E0.top"),sQuery(id+"F0.wireOp",EDGE,"E0.left"),sQuery(id+"F0.wireOp",EDGE,"E0.right"),sQuery(id+"F0.wireOp",EDGE,"E3")])],"isStart":true}),makeQuery(id+"F14.opExtrude","CAP_FACE",FACE,{"disambiguationData":[OSD([sQuery(id+"F10.wireOp",EDGE,"E8.sketch_text.stroke-0"),sQuery(id+"F10.wireOp",EDGE,"E8.sketch_text.stroke-1"),sQuery(id+"F10.wireOp",EDGE,"E8.sketch_text.stroke-2"),sQuery(id+"F10.wireOp",EDGE,"E8.sketch_text.stroke-3"),sQuery(id+"F10.wireOp",EDGE,"E8.sketch_text.stroke-4"),sQuery(id+"F10.wireOp",EDGE,"E8.sketch_text.stroke-5"),sQuery(id+"F10.wireOp",EDGE,"E8.sketch_text.stroke-6"),sQuery(id+"F10.wireOp",EDGE,"E8.sketch_text.stroke-7"),sQuery(id+"F10.wireOp",EDGE,"E8.sketch_text.stroke-8"),sQuery(id+"F10.wireOp",EDGE,"E8.sketch_text.stroke-9"),sQuery(id+"F10.wireOp",EDGE,"E8.sketch_text.stroke-10"),sQuery(id+"F10.wireOp",EDGE,"E8.sketch_text.stroke-11"),sQuery(id+"F10.wireOp",EDGE,"E8.sketch_text.stroke-12"),sQuery(id+"F10.wireOp",EDGE,"E8.sketch_text.stroke-13"),sQuery(id+"F10.wireOp",EDGE,"E8.sketch_text.stroke-14"),sQuery(id+"F10.wireOp",EDGE,"E8.sketch_text.stroke-15"),sQuery(id+"F10.wireOp",EDGE,"E8.sketch_text.stroke-16"),sQuery(id+"F10.wireOp",EDGE,"E8.sketch_text.stroke-17"),sQuery(id+"F10.wireOp",EDGE,"E8.sketch_text.stroke-18"),sQuery(id+"F10.wireOp",EDGE,"E8.sketch_text.stroke-19"),sQuery(id+"F10.wireOp",EDGE,"E8.sketch_text.stroke-20"),sQuery(id+"F10.wireOp",EDGE,"E8.sketch_text.stroke-21"),sQuery(id+"F10.wireOp",EDGE,"E8.sketch_text.stroke-22"),sQuery(id+"F10.wireOp",EDGE,"E8.sketch_text.stroke-23"),sQuery(id+"F10.wireOp",EDGE,"E8.sketch_text.stroke-24"),sQuery(id+"F10.wireOp",EDGE,"E8.sketch_text.stroke-25"),sQuery(id+"F10.wireOp",EDGE,"E8.sketch_text.stroke-26"),sQuery(id+"F10.wireOp",EDGE,"E8.sketch_text.stroke-27")])],"isStart":true})]});
            fillet(context, id + "F27", {"entities" : qUnion([Q0]), "radius" : 3 * mm, "tangentPropagation" : true, "allowEdgeOverflow" : false});
        }
    });
